# Revit family: Lichtband B -Mid Section
name_source: partatom
category: Windows
revit_build: Autodesk Revit 2014 (Build: 20130308_1515(x64)
units: mm (PartAtom-declared; Revit-internal decimal feet)

## types (4) — shared parameters
Adjustable Flap Width = 300 mm
Clear Length = 2100 mm  [stored 6.88976 ft]
Clear Width = 2000 mm  [stored 6.56168 ft]
Kurb Height = 300 mm
Opening Width = 1200 mm
Primary Material = Lamilux-White
Product data url = http://lamilux.bimobject.com
Radius = 2110 mm  [stored 6.92257 ft]
Secondary Material = Lamilux- Glass

## per-type parameters (varying)
| type | Asymmetric Flap Width | DFWO | FSWO | Flap Symmetry | SFWO | With Opening |
| Single Flap | 300 mm | No | No | No | Yes | Yes |
| Double Flap | 600 mm | Yes | Yes | Yes | No | Yes |
| Asymmetrical Flap | 300 mm | Yes | No | No | No | Yes |
| Without Opening | 300 mm | No | No | No | No | No |

type visibility flags (boolean, named after types; folded from table):
- Single Flap: Yes: Single Flap
- Double Flap: Yes: Double Flap
- Asymmetrical Flap: Yes: Double Flap
- Without Opening: Yes: Without Opening

note: [stored X ft] marks values corroborated as IEEE doubles in the binary element streams (Revit-internal decimal feet)

## geometry (parser evidence)
native form markers: Sweep x9
no freeform markers — native parametric forms only
